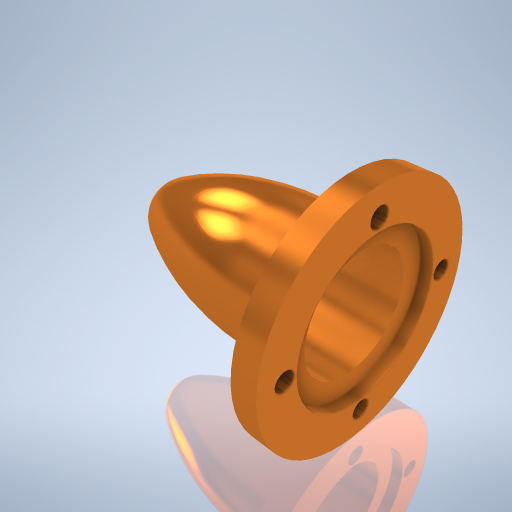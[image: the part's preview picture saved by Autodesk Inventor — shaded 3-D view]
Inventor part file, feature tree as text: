
AUTODESK INVENTOR PART (.ipt)
format: ipt  version: 2024.2 (Build 282272000, 272)  size: 337,408 bytes
history: native  units: mm
features: sketch x4, revolve x2, plane x1, hole x1, pattern_circular x1, extrude x1, projected_geometry x1
ambient origin geometry x8: Origin, YZ Plane, XZ Plane, XY Plane, X Axis, Y Axis, Z Axis, Center Point
bodies: Body1 (feature_tree)
feature tree (11):
  revolve  "Umdrehung2"
  plane  "Arbeitsebene1"
  revolve  "Umdrehung3"
  hole  "Bohrung1"  [1 undecoded]
  pattern_circular  "Runde Anordnung1"  [2 undecoded]
  extrude  "Extrusion1"  Depth=36.09589mm
  sketch  "Skizze2"  dims[d12=39.0mm d13=4.0mm]
  sketch  "Skizze3"  dims[d14=22.0mm]
  projected_geometry  "Projizierte Kontur1"
  sketch  "Skizze4"  dims[d15=39.0mm]
  sketch  "Skizze5"  dims[d16=33.0mm d17=10.54mm d18=36.09589mm d19=90.0deg d21=0.0mm d22=7.9mm d23=4.5mm d24=45.5mm d25=19.0mm d26=90.0deg d27=15.0mm d28=3.2mm d29=6.0mm d30=4.0mm d31=2.0mm d32=90.0deg d33=8.0mm d34=0.0mm d35=40.0mm d36=360.0deg d38=26.0mm d39=2.0mm d40=0.0mm]
note: 3 required parameter values undecoded (feature->parameter linkage not recoverable at this tier; creation-order binding heuristic only, values carry confidence <= 0.55)
